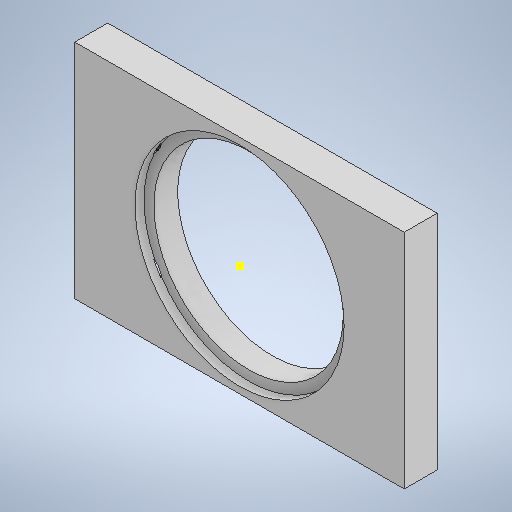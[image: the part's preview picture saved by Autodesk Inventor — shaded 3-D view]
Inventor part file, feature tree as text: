
AUTODESK INVENTOR PART (.ipt)
format: ipt  version: 2025 (Build 290162000, 162)  size: 269,824 bytes
history: native  units: mm
features: sketch x3, hole x2, extrude x1
ambient origin geometry x8: Origin, YZ Plane, XZ Plane, XY Plane, X Axis, Y Axis, Z Axis, Center Point
bodies: 实体1 (feature_tree)
feature tree (6):
  sketch  "草图1"  dims[d0=51.9mm d1=30.0mm]
  extrude  "拉伸1"  Depth=30.0mm
  hole  "孔1"  [1 undecoded]
  hole  "孔2"  [1 undecoded]
  sketch  "草图3"  dims[d8=27.0mm d9=4.0mm d10=0.0mm d11=5.0mm d12=5.0mm d13=5.0mm d14=4.94mm d15=6.0mm d16=4.0mm d17=2.0mm d18=90.0deg d19=3.0mm d20=0.0mm d21=25.4mm d22=6.0mm d23=4.0mm d24=2.0mm d25=90.0deg d26=1.1mm d27=0.0mm]
  sketch  "草图2"  dims[d6=23.0mm d7=40.0mm]
note: 2 required parameter values undecoded (feature->parameter linkage not recoverable at this tier; creation-order binding heuristic only, values carry confidence <= 0.55)
